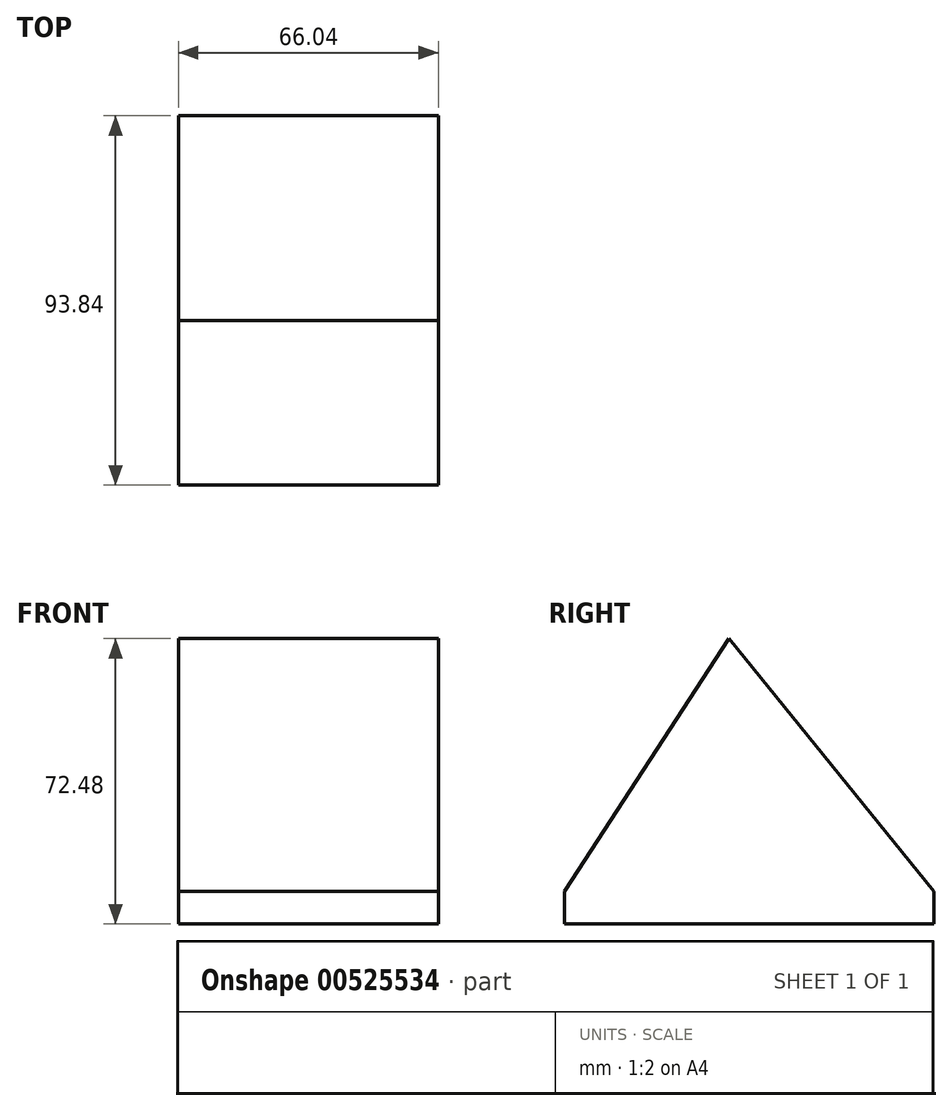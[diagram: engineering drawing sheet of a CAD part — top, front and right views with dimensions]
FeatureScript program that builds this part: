
annotation { "Feature Type Name" : "Feature", "Feature Type Description" : "" }
export const myFeature = defineFeature(function(context is Context, id is Id, definition is map)
    precondition{}
    {
        {
            var Q0;
            Q0=qCreatedBy(makeId("Right.planeOp"),FACE);
            var sketch = newSketch(context, id + "F0", { "sketchPlane" : qUnion([Q0])});
            skLineSegment(sketch, "E0.bottom", {"start": v(46.92, 4.1) * mm, "end": v(-46.92, 4.1) * mm});
            skLineSegment(sketch, "E0.top", {"start": v(46.92, -4.1) * mm, "end": v(-46.92, -4.1) * mm});
            skLineSegment(sketch, "E0.left", {"start": v(46.92, 4.1) * mm, "end": v(46.92, -4.1) * mm});
            skLineSegment(sketch, "E0.right", {"start": v(-46.92, 4.1) * mm, "end": v(-46.92, -4.1) * mm});
            skPoint(sketch, "E0.middle", {"position": v(0, 0) * mm});
            skLineSegment(sketch, "E1", {"start": v(46.92, 4.1) * mm, "end": v(-5.07, 68.38) * mm});
            skLineSegment(sketch, "E2", {"start": v(-5.07, 68.38) * mm, "end": v(-46.92, 4.1) * mm});
            skSolve(sketch);
        }
        {
            var Q0;
            Q0 = qSketchRegion(id + "F0", true);
            extrude(context, id + "F1", {"entities" : qUnion([Q0]), "depth" : 66.04 * mm, "offsetDistance" : 25.4 * mm});
        }
    });
